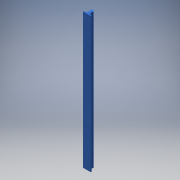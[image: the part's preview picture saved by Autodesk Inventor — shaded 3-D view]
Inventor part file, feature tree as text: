
AUTODESK INVENTOR PART (.ipt)
format: ipt  version: 2018 (Build 220112000, 112)  size: 140,800 bytes
history: native  units: mm
features: sketch x2, other x1, extrude x1, hole x1
ambient origin geometry x8: Origin, YZ Plane, XZ Plane, XY Plane, X Axis, Y Axis, Z Axis, Center Point
bodies: Body1 (feature_tree)
feature tree (5):
  other  "Sólido1"
  extrude  "Extrusão1"  Depth=25.0mm
  hole  "Furo1"  [1 undecoded]
  sketch  "Esboço1"  dims[d6=16.0mm d7=25.0mm]
  sketch  "Esboço3"  dims[d8=18.5mm d9=11.7mm d10=8.0mm d11=30.0deg d12=30.0deg d13=5.0mm d14=40.0mm d15=700.0mm d16=0.0mm d18=15.0mm d19=15.0mm d20=5.5mm d21=5.5mm d22=20.0mm d28=5.5mm d29=6.0mm d30=4.0mm d31=2.0mm d32=90.0deg d33=8.0mm d34=20.594885mm]
note: 1 required parameter value undecoded (feature->parameter linkage not recoverable at this tier; creation-order binding heuristic only, values carry confidence <= 0.55)
